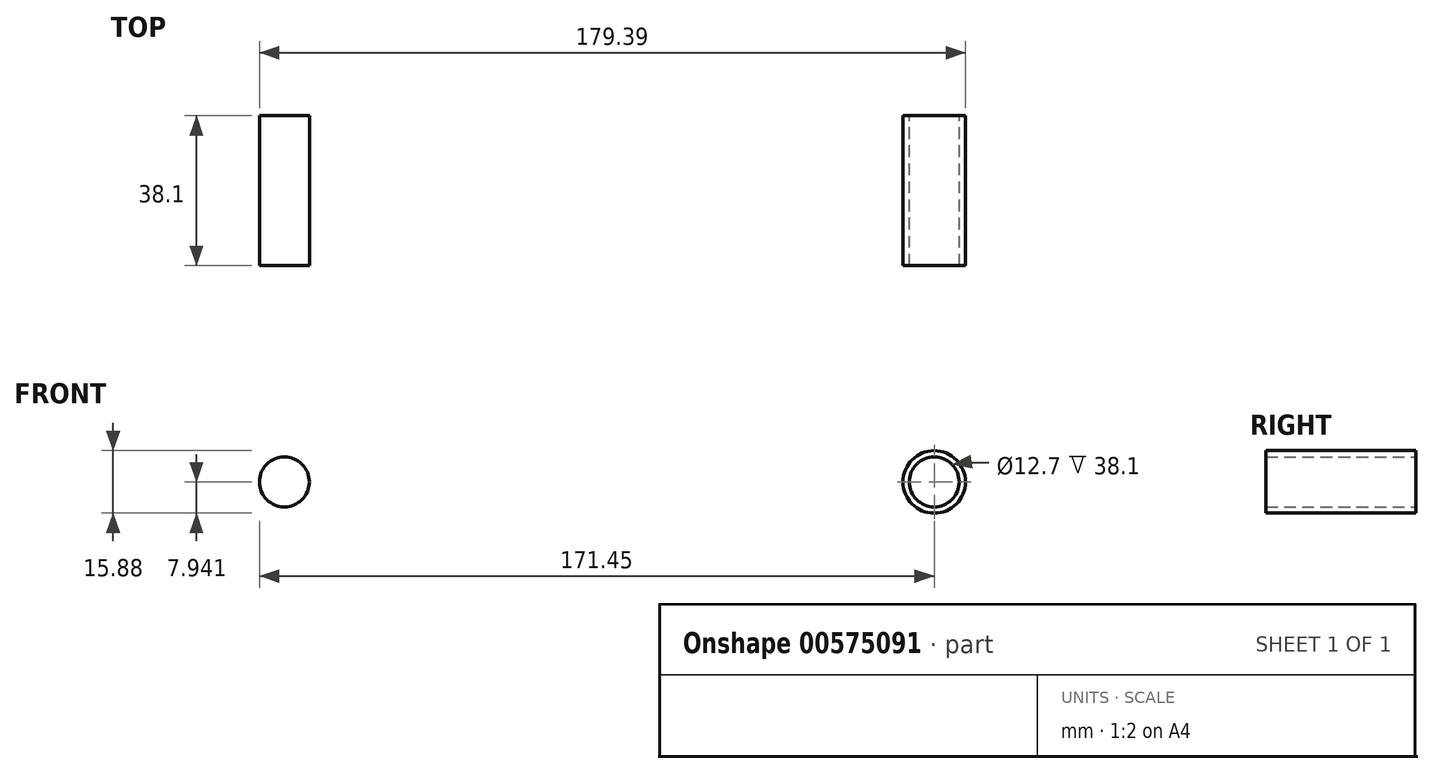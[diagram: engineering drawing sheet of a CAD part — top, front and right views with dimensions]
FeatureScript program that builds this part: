
annotation { "Feature Type Name" : "Feature", "Feature Type Description" : "" }
export const myFeature = defineFeature(function(context is Context, id is Id, definition is map)
    precondition{}
    {
        {
            var Q0;
            Q0=qCreatedBy(makeId("Front.planeOp"),FACE);
            var sketch = newSketch(context, id + "F0", { "sketchPlane" : qUnion([Q0])});
            skLineSegment(sketch, "E0", {"start": v(0, 45.16) * mm, "end": v(0, -51.97) * mm, "construction": true});
            skArc(sketch, "E1", {"start": v(0, -25.07) * mm, "mid": v(14.44, -31.7) * mm, "end": v(18.84, -46.96) * mm});
            skLineSegment(sketch, "E2", {"start": v(90.87, 4.77) * mm, "end": v(88.98, 5.9) * mm});
            skLineSegment(sketch, "E3", {"start": v(1.52, 34.14) * mm, "end": v(0, 34.14) * mm});
            skLineSegment(sketch, "E4.MirrorCS", {"start": v(-1.52, 34.14) * mm, "end": v(0, 34.14) * mm});
            skLineSegment(sketch, "E5.MirrorCS", {"start": v(-90.87, 4.77) * mm, "end": v(-88.98, 5.9) * mm});
            skCircle(sketch, "E6", {"center": v(50.8, 38.43) * mm, "radius": 12.7 * mm});
            skCircle(sketch, "E7", {"center": v(0, 3.5) * mm, "radius": 12.7 * mm});
            skCircle(sketch, "E8.MirrorC", {"center": v(-50.8, 38.43) * mm, "radius": 12.7 * mm});
            skLineSegment(sketch, "E9", {"start": v(18.84, -46.96) * mm, "end": v(18.84, -50.47) * mm});
            skLineSegment(sketch, "E10", {"start": v(18.84, -50.47) * mm, "end": v(28.95, -50.47) * mm});
            skArc(sketch, "E11", {"start": v(28.95, -50.47) * mm, "mid": v(39.28, -46.57) * mm, "end": v(44.45, -36.82) * mm});
            skArc(sketch, "E12", {"start": v(44.45, -36.82) * mm, "mid": v(45.3, -33.9) * mm, "end": v(47.03, -31.42) * mm});
            skLineSegment(sketch, "E13", {"start": v(47.03, -31.42) * mm, "end": v(82.55, -31.42) * mm});
            skArc(sketch, "E14", {"start": v(82.55, -31.42) * mm, "mid": v(101.12, -16.64) * mm, "end": v(90.87, 4.77) * mm});
            skArc(sketch, "E15.MirrorCS", {"start": v(0, -25.07) * mm, "mid": v(-14.44, -31.7) * mm, "end": v(-18.84, -46.96) * mm});
            skLineSegment(sketch, "E16.MirrorCS", {"start": v(-18.84, -46.96) * mm, "end": v(-18.84, -50.47) * mm});
            skLineSegment(sketch, "E17.MirrorCS", {"start": v(-18.84, -50.47) * mm, "end": v(-28.95, -50.47) * mm});
            skArc(sketch, "E18.MirrorCS", {"start": v(-28.95, -50.47) * mm, "mid": v(-39.28, -46.57) * mm, "end": v(-44.45, -36.82) * mm});
            skArc(sketch, "E19.MirrorCS", {"start": v(-44.45, -36.82) * mm, "mid": v(-45.3, -33.9) * mm, "end": v(-47.03, -31.42) * mm});
            skLineSegment(sketch, "E20.MirrorCS", {"start": v(-47.03, -31.42) * mm, "end": v(-82.55, -31.42) * mm});
            skArc(sketch, "E21.MirrorCS", {"start": v(-82.55, -31.42) * mm, "mid": v(-101.12, -16.64) * mm, "end": v(-90.87, 4.77) * mm});
            skCircle(sketch, "E22", {"center": v(82.55, -12.37) * mm, "radius": 6.35 * mm});
            skCircle(sketch, "E23.MirrorC", {"center": v(-82.55, -12.37) * mm, "radius": 6.35 * mm});
            skArc(sketch, "E24", {"start": v(-88.98, 5.9) * mm, "mid": v(-87.37, 7.47) * mm, "end": v(-86.65, 9.6) * mm});
            skLineSegment(sketch, "E25", {"start": v(-86.65, 9.6) * mm, "end": v(-86.65, 41.8) * mm});
            skArc(sketch, "E26", {"start": v(-86.65, 41.8) * mm, "mid": v(-50.8, 77.66) * mm, "end": v(-14.95, 41.8) * mm});
            skArc(sketch, "E27", {"start": v(-14.95, 41.8) * mm, "mid": v(-12.77, 35.58) * mm, "end": v(-7.18, 32.08) * mm});
            skLineSegment(sketch, "E28", {"start": v(-7.18, 32.08) * mm, "end": v(1.52, 32.08) * mm});
            skLineSegment(sketch, "E29.MirrorCS", {"start": v(7.18, 32.08) * mm, "end": v(-1.52, 32.08) * mm});
            skLineSegment(sketch, "E30.MirrorCS", {"start": v(86.65, 9.6) * mm, "end": v(86.65, 41.8) * mm});
            skArc(sketch, "E31.MirrorCS", {"start": v(88.98, 5.9) * mm, "mid": v(87.37, 7.47) * mm, "end": v(86.65, 9.6) * mm});
            skArc(sketch, "E32.MirrorCS", {"start": v(86.65, 41.8) * mm, "mid": v(50.8, 77.66) * mm, "end": v(14.95, 41.8) * mm});
            skArc(sketch, "E33.MirrorCS", {"start": v(14.95, 41.8) * mm, "mid": v(12.77, 35.58) * mm, "end": v(7.18, 32.08) * mm});
            skCircle(sketch, "E34", {"center": v(-82.55, -12.37) * mm, "radius": 7.94 * mm});
            skCircle(sketch, "E35", {"center": v(82.55, -12.37) * mm, "radius": 7.94 * mm});
            skSolve(sketch);
        }
        {
            var Q0;
            Q0=makeQuery(id+"F0.imprint","IMPRINT",FACE,{"disambiguationData":[TD([[makeQuery(id+"F0.imprint","IMPRINT",EDGE,{"derivedFrom":sQuery(id+"F0.wireOp",EDGE,"E1")}),1.0]])]});
            var Q1;
            Q1=makeQuery(id+"F0.imprint","IMPRINT",FACE,{"disambiguationData":[TD([[makeQuery(id+"F0.imprint","IMPRINT",EDGE,{"derivedFrom":sQuery(id+"F0.wireOp",EDGE,"E23.MirrorC")}),1.0]])]});
            var Q2;
            Q2=makeQuery(id+"F0.imprint","IMPRINT",FACE,{"disambiguationData":[TD([[makeQuery(id+"F0.imprint","IMPRINT",EDGE,{"derivedFrom":sQuery(id+"F0.wireOp",EDGE,"E22")}),-1.0]])]});
            extrude(context, id + "F1", {"entities" : qUnion([Q0, Q1, Q2]), "depth" : 12.7 * mm, "offsetDistance" : 25.4 * mm});
        }
        {
            var Q0;
            Q0=makeQuery(id+"F0.imprint","IMPRINT",FACE,{"disambiguationData":[TD([[makeQuery(id+"F0.imprint","IMPRINT",EDGE,{"derivedFrom":sQuery(id+"F0.wireOp",EDGE,"E23.MirrorC")}),1.0]])]});
            var Q1;
            Q1=makeQuery(id+"F0.imprint","IMPRINT",FACE,{"disambiguationData":[TD([[makeQuery(id+"F0.imprint","IMPRINT",EDGE,{"derivedFrom":sQuery(id+"F0.wireOp",EDGE,"E22")}),-1.0]])]});
            extrude(context, id + "F2", {"entities" : qUnion([Q0, Q1]), "operationType" : NewBodyOperationType.ADD, "depth" : 38.1 * mm, "offsetDistance" : 25.4 * mm});
        }
    });
